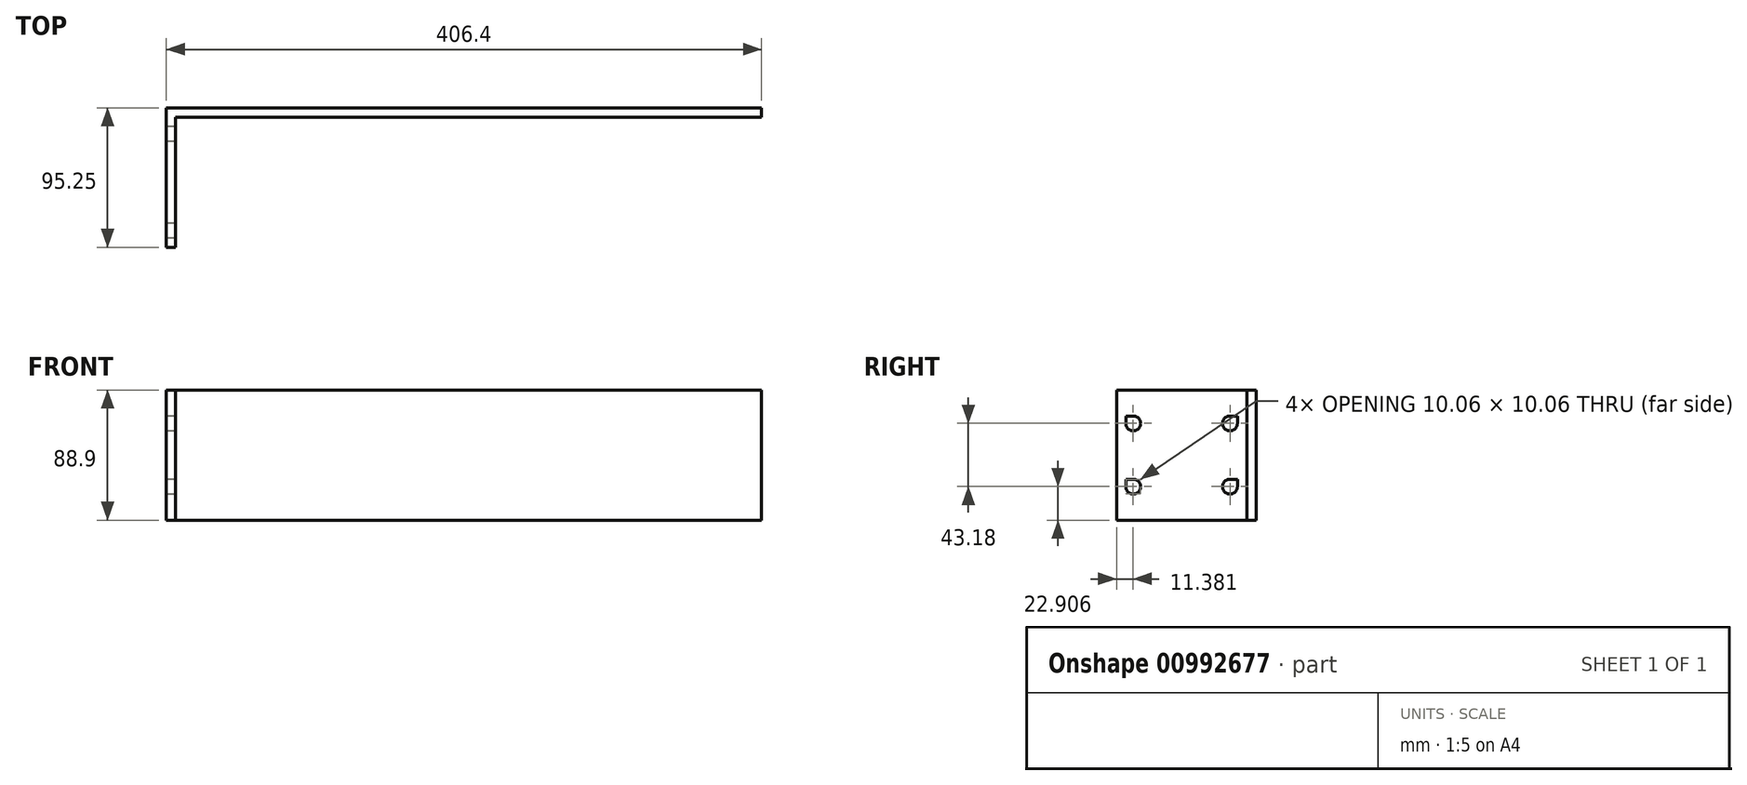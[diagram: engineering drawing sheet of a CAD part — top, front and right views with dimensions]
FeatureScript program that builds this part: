
annotation { "Feature Type Name" : "Feature", "Feature Type Description" : "" }
export const myFeature = defineFeature(function(context is Context, id is Id, definition is map)
    precondition{}
    {
        {
            var Q0;
            Q0=qCreatedBy(makeId("Front.planeOp"),FACE);
            var sketch = newSketch(context, id + "F0", { "sketchPlane" : qUnion([Q0])});
            skLineSegment(sketch, "E0.bottom", {"start": v(-52.08, 63.37) * mm, "end": v(354.32, 63.37) * mm});
            skLineSegment(sketch, "E0.top", {"start": v(-52.08, -25.53) * mm, "end": v(354.32, -25.53) * mm});
            skLineSegment(sketch, "E0.left", {"start": v(-52.08, 63.37) * mm, "end": v(-52.08, -25.53) * mm});
            skLineSegment(sketch, "E0.right", {"start": v(354.32, 63.37) * mm, "end": v(354.32, -25.53) * mm});
            skSolve(sketch);
        }
        {
            var Q0;
            Q0=makeQuery(id+"F0.imprint","IMPRINT",FACE,{"disambiguationData":[TD([[makeQuery(id+"F0.imprint","IMPRINT",EDGE,{"derivedFrom":sQuery(id+"F0.wireOp",EDGE,"E0.bottom")}),-1.0]])]});
            extrude(context, id + "F1", {"entities" : qUnion([Q0]), "depth" : 6.35 * mm, "offsetDistance" : 25.4 * mm});
        }
        {
            var Q0;
            Q0=makeQuery(id+"F1.opExtrude","CAP_FACE",FACE,{"disambiguationData":[OSD([sQuery(id+"F0.wireOp",EDGE,"E0.bottom"),sQuery(id+"F0.wireOp",EDGE,"E0.top"),sQuery(id+"F0.wireOp",EDGE,"E0.left"),sQuery(id+"F0.wireOp",EDGE,"E0.right")])],"isStart":false});
            var sketch = newSketch(context, id + "F2", { "sketchPlane" : qUnion([Q0])});
            skLineSegment(sketch, "E1.bottom", {"start": v(-52.08, 63.37) * mm, "end": v(-45.73, 63.37) * mm});
            skLineSegment(sketch, "E1.top", {"start": v(-52.08, -25.53) * mm, "end": v(-45.73, -25.53) * mm});
            skLineSegment(sketch, "E1.left", {"start": v(-52.08, 63.37) * mm, "end": v(-52.08, -25.53) * mm});
            skLineSegment(sketch, "E1.right", {"start": v(-45.73, 63.37) * mm, "end": v(-45.73, -25.53) * mm});
            skSolve(sketch);
        }
        {
            var Q0;
            Q0=makeQuery(id+"F2.imprint","IMPRINT",FACE,{"disambiguationData":[TD([[makeQuery(id+"F2.imprint","IMPRINT",EDGE,{"derivedFrom":sQuery(id+"F2.wireOp",EDGE,"E1.bottom")}),-1.0]])]});
            extrude(context, id + "F3", {"entities" : qUnion([Q0]), "operationType" : NewBodyOperationType.ADD, "depth" : 88.9 * mm, "offsetDistance" : 25.4 * mm});
        }
        {
            var Q0;
            Q0=makeQuery(id+"F3.boolean.opBoolean","MERGE",FACE,{"derivedFrom":[makeQuery(id+"F1.opExtrude","SWEPT_FACE",FACE,{"disambiguationData":[OSD([sQuery(id+"F0.wireOp",EDGE,"E0.left")])]}),makeQuery(id+"F3.opExtrude","SWEPT_FACE",FACE,{"disambiguationData":[OSD([sQuery(id+"F2.wireOp",EDGE,"E1.left")])]})]});
            var sketch = newSketch(context, id + "F4", { "sketchPlane" : qUnion([Q0])});
            skLineSegment(sketch, "E2.bottom", {"start": v(95.25, 63.37) * mm, "end": v(88.9, 63.37) * mm});
            skLineSegment(sketch, "E2.top", {"start": v(95.25, -25.53) * mm, "end": v(88.9, -25.53) * mm});
            skLineSegment(sketch, "E2.left", {"start": v(95.25, 63.37) * mm, "end": v(95.25, -25.53) * mm});
            skLineSegment(sketch, "E2.right", {"start": v(88.9, 63.37) * mm, "end": v(88.9, -25.53) * mm});
            skLineSegment(sketch, "E3.bottom", {"start": v(0, 63.37) * mm, "end": v(12.7, 63.37) * mm});
            skLineSegment(sketch, "E3.top", {"start": v(0, -25.53) * mm, "end": v(12.7, -25.53) * mm});
            skLineSegment(sketch, "E3.left", {"start": v(0, 63.37) * mm, "end": v(0, -25.53) * mm});
            skLineSegment(sketch, "E3.right", {"start": v(12.7, 63.37) * mm, "end": v(12.7, -25.53) * mm});
            skLineSegment(sketch, "E4.bottom", {"start": v(12.7, 63.37) * mm, "end": v(88.9, 63.37) * mm});
            skLineSegment(sketch, "E4.top", {"start": v(12.7, 45.59) * mm, "end": v(88.9, 45.59) * mm});
            skLineSegment(sketch, "E4.left", {"start": v(12.7, 63.37) * mm, "end": v(12.7, 45.59) * mm});
            skLineSegment(sketch, "E4.right", {"start": v(88.9, 63.37) * mm, "end": v(88.9, 45.59) * mm});
            skLineSegment(sketch, "E5.top", {"start": v(12.7, 35.43) * mm, "end": v(88.9, 35.43) * mm});
            skLineSegment(sketch, "E5.left", {"start": v(12.7, 45.59) * mm, "end": v(12.7, 35.43) * mm});
            skLineSegment(sketch, "E5.right", {"start": v(88.9, 45.59) * mm, "end": v(88.9, 35.43) * mm});
            skLineSegment(sketch, "E6.top", {"start": v(12.7, 2.4) * mm, "end": v(88.9, 2.4) * mm});
            skLineSegment(sketch, "E6.left", {"start": v(12.7, 35.43) * mm, "end": v(12.7, 2.4) * mm});
            skLineSegment(sketch, "E6.right", {"start": v(88.9, 35.43) * mm, "end": v(88.9, 2.4) * mm});
            skLineSegment(sketch, "E7.top", {"start": v(12.7, -7.75) * mm, "end": v(88.9, -7.75) * mm});
            skLineSegment(sketch, "E7.left", {"start": v(12.7, 2.4) * mm, "end": v(12.7, -7.75) * mm});
            skLineSegment(sketch, "E7.right", {"start": v(88.9, 2.4) * mm, "end": v(88.9, -7.75) * mm});
            skLineSegment(sketch, "E8.top", {"start": v(12.7, -25.53) * mm, "end": v(88.9, -25.53) * mm});
            skLineSegment(sketch, "E8.left", {"start": v(12.7, -7.75) * mm, "end": v(12.7, -25.53) * mm});
            skLineSegment(sketch, "E8.right", {"start": v(88.9, -7.75) * mm, "end": v(88.9, -25.53) * mm});
            skLineSegment(sketch, "E9", {"start": v(12.7, 45.59) * mm, "end": v(17.78, 45.59) * mm});
            skLineSegment(sketch, "E10", {"start": v(17.78, 45.59) * mm, "end": v(17.78, 35.43) * mm});
            skLineSegment(sketch, "E11", {"start": v(17.78, 35.43) * mm, "end": v(88.9, 35.43) * mm});
            skLineSegment(sketch, "E12", {"start": v(88.9, 45.59) * mm, "end": v(83.82, 45.59) * mm});
            skLineSegment(sketch, "E13", {"start": v(83.82, 45.59) * mm, "end": v(83.82, 35.43) * mm});
            skLineSegment(sketch, "E14", {"start": v(12.7, 2.4) * mm, "end": v(17.78, 2.4) * mm});
            skLineSegment(sketch, "E15", {"start": v(17.78, 2.4) * mm, "end": v(17.78, -7.75) * mm});
            skLineSegment(sketch, "E16", {"start": v(17.78, -7.75) * mm, "end": v(88.9, -7.75) * mm});
            skLineSegment(sketch, "E17", {"start": v(88.9, 2.4) * mm, "end": v(83.82, 2.4) * mm});
            skLineSegment(sketch, "E18", {"start": v(83.82, 2.4) * mm, "end": v(83.82, -7.75) * mm});
            skCircle(sketch, "E19", {"center": v(17.78, 40.5) * mm, "radius": 5.08 * mm});
            skCircle(sketch, "E20", {"center": v(17.78, -2.67) * mm, "radius": 5.08 * mm});
            skCircle(sketch, "E21", {"center": v(83.82, 40.5) * mm, "radius": 5.08 * mm});
            skCircle(sketch, "E22", {"center": v(83.82, -2.67) * mm, "radius": 5.08 * mm});
            skSolve(sketch);
        }
        {
            var Q0;
            {var subQ0=sQuery(id+"F4.wireOp",EDGE,"E10");Q0=makeQuery(id+"F4.imprint","IMPRINT",FACE,{"disambiguationData":[TD([[makeQuery(id+"F4.imprint","IMPRINT",EDGE,{"derivedFrom":subQ0}),-1.0]])]});}
            var Q1;
            {var subQ0=sQuery(id+"F4.wireOp",EDGE,"E10");Q1=makeQuery(id+"F4.imprint","IMPRINT",FACE,{"disambiguationData":[TD([[makeQuery(id+"F4.imprint","IMPRINT",EDGE,{"derivedFrom":subQ0}),1.0]])]});}
            var Q2;
            {var subQ0=sQuery(id+"F4.wireOp",EDGE,"E15");Q2=makeQuery(id+"F4.imprint","IMPRINT",FACE,{"disambiguationData":[TD([[makeQuery(id+"F4.imprint","IMPRINT",EDGE,{"derivedFrom":subQ0}),-1.0]])]});}
            var Q3;
            {var subQ0=sQuery(id+"F4.wireOp",EDGE,"E15");Q3=makeQuery(id+"F4.imprint","IMPRINT",FACE,{"disambiguationData":[TD([[makeQuery(id+"F4.imprint","IMPRINT",EDGE,{"derivedFrom":subQ0}),1.0]])]});}
            var Q4;
            {var subQ0=sQuery(id+"F4.wireOp",EDGE,"E4.top");Q4=makeQuery(id+"F4.imprint","IMPRINT",FACE,{"disambiguationData":[TD([[makeQuery(id+"F4.imprint","IMPRINT",EDGE,{"derivedFrom":subQ0}),-1.0]])]});}
            var Q5;
            {var subQ0=sQuery(id+"F4.wireOp",EDGE,"E13");Q5=makeQuery(id+"F4.imprint","IMPRINT",FACE,{"disambiguationData":[TD([[makeQuery(id+"F4.imprint","IMPRINT",EDGE,{"derivedFrom":subQ0}),-1.0]])]});}
            var Q6;
            {var subQ0=sQuery(id+"F4.wireOp",EDGE,"E13");Q6=makeQuery(id+"F4.imprint","IMPRINT",FACE,{"disambiguationData":[TD([[makeQuery(id+"F4.imprint","IMPRINT",EDGE,{"derivedFrom":subQ0}),1.0]])]});}
            var Q7;
            {var subQ0=sQuery(id+"F4.wireOp",EDGE,"E6.top");Q7=makeQuery(id+"F4.imprint","IMPRINT",FACE,{"disambiguationData":[TD([[makeQuery(id+"F4.imprint","IMPRINT",EDGE,{"derivedFrom":subQ0}),-1.0]])]});}
            var Q8;
            {var subQ0=sQuery(id+"F4.wireOp",EDGE,"E18");Q8=makeQuery(id+"F4.imprint","IMPRINT",FACE,{"disambiguationData":[TD([[makeQuery(id+"F4.imprint","IMPRINT",EDGE,{"derivedFrom":subQ0}),-1.0]])]});}
            var Q9;
            {var subQ0=sQuery(id+"F4.wireOp",EDGE,"E18");Q9=makeQuery(id+"F4.imprint","IMPRINT",FACE,{"disambiguationData":[TD([[makeQuery(id+"F4.imprint","IMPRINT",EDGE,{"derivedFrom":subQ0}),1.0]])]});}
            extrude(context, id + "F5", {"entities" : qUnion([Q0, Q1, Q2, Q3, Q4, Q5, Q6, Q7, Q8, Q9]), "operationType" : NewBodyOperationType.REMOVE, "oppositeDirection" : true, "depth" : 25.4 * mm, "offsetDistance" : 25.4 * mm});
        }
    });
